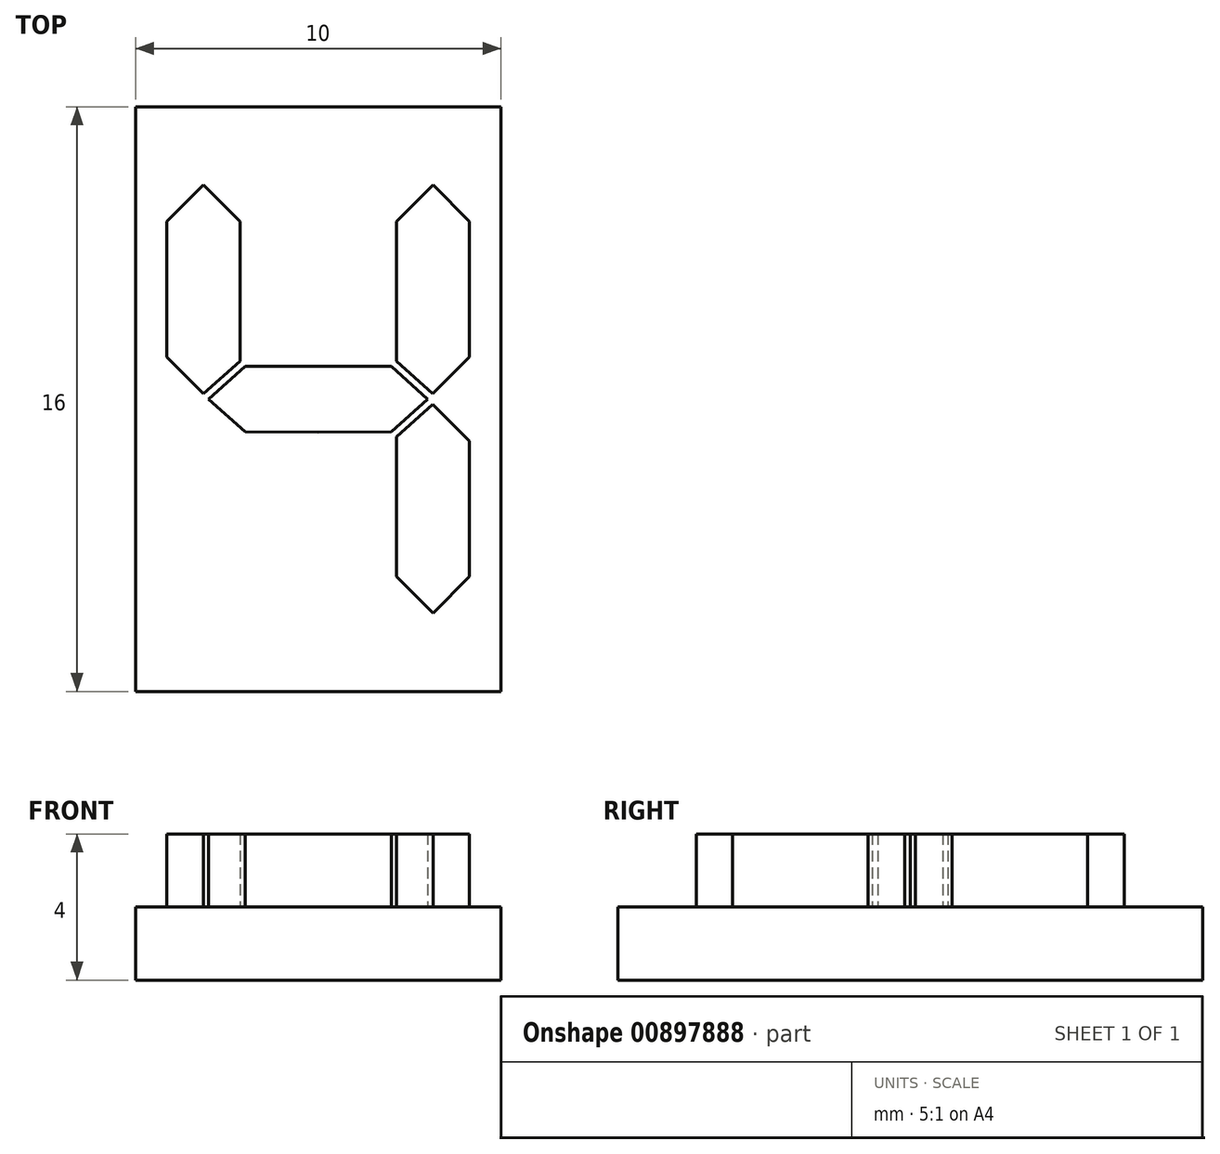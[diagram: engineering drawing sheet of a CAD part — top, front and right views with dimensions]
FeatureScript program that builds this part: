
annotation { "Feature Type Name" : "Feature", "Feature Type Description" : "" }
export const myFeature = defineFeature(function(context is Context, id is Id, definition is map)
    precondition{}
    {
        {
            var Q0;
            Q0=qCreatedBy(makeId("Top.planeOp"),FACE);
            var sketch = newSketch(context, id + "F0", { "sketchPlane" : qUnion([Q0])});
            skLineSegment(sketch, "E0.bottom", {"start": v(5, -8) * mm, "end": v(-5, -8) * mm});
            skLineSegment(sketch, "E0.top", {"start": v(5, 8) * mm, "end": v(-5, 8) * mm});
            skLineSegment(sketch, "E0.left", {"start": v(5, -8) * mm, "end": v(5, 8) * mm});
            skLineSegment(sketch, "E0.right", {"start": v(-5, -8) * mm, "end": v(-5, 8) * mm});
            skPoint(sketch, "E0.middle", {"position": v(0, 0) * mm});
            skSolve(sketch);
        }
        {
            var Q0;
            Q0=makeQuery(id+"F0.imprint","IMPRINT",FACE,{"disambiguationData":[TD([[makeQuery(id+"F0.imprint","IMPRINT",EDGE,{"derivedFrom":sQuery(id+"F0.wireOp",EDGE,"E0.bottom")}),-1.0]])]});
            extrude(context, id + "F1", {"entities" : qUnion([Q0]), "depth" : 2 * mm, "offsetDistance" : 25 * mm});
        }
        {
            var Q0;
            Q0=makeQuery(id+"F1.opExtrude","CAP_FACE",FACE,{"disambiguationData":[OSD([sQuery(id+"F0.wireOp",EDGE,"E0.bottom"),sQuery(id+"F0.wireOp",EDGE,"E0.top"),sQuery(id+"F0.wireOp",EDGE,"E0.left"),sQuery(id+"F0.wireOp",EDGE,"E0.right")])],"isStart":false});
            var sketch = newSketch(context, id + "F2", { "sketchPlane" : qUnion([Q0])});
            skLineSegment(sketch, "E1", {"start": v(-3, 8) * mm, "end": v(-3, -8) * mm, "construction": true});
            skLineSegment(sketch, "E2.0.1.0", {"start": v(-5, 6) * mm, "end": v(5, 6) * mm, "construction": true});
            skLineSegment(sketch, "E2.direction2", {"start": v(-5, 7) * mm, "end": v(-5, 6) * mm, "construction": true});
            skLineSegment(sketch, "E3.1.0.0", {"start": v(-2, 8) * mm, "end": v(-2, -8) * mm, "construction": true});
            skLineSegment(sketch, "E3.3.0.0", {"start": v(0, 8) * mm, "end": v(0, -8) * mm, "construction": true});
            skLineSegment(sketch, "E3.direction1", {"start": v(-3, -8) * mm, "end": v(-2, -8) * mm, "construction": true});
            skLineSegment(sketch, "E4", {"start": v(-2, 7) * mm, "end": v(-3, 6) * mm, "construction": true});
            skLineSegment(sketch, "E5", {"start": v(-3, 6) * mm, "end": v(-2, 5) * mm, "construction": true});
            skLineSegment(sketch, "E6", {"start": v(-2, 5) * mm, "end": v(0, 5) * mm, "construction": true});
            skLineSegment(sketch, "E7", {"start": v(-2, 7) * mm, "end": v(0, 7) * mm, "construction": true});
            skLineSegment(sketch, "E8.0", {"start": v(-3.14, 5.86) * mm, "end": v(-2.14, 4.86) * mm});
            skLineSegment(sketch, "E9", {"start": v(-2.14, 4.86) * mm, "end": v(-2.14, 1.03) * mm});
            skLineSegment(sketch, "E10.0", {"start": v(-4.14, 4.86) * mm, "end": v(-4.14, 1.15) * mm});
            skLineSegment(sketch, "E11", {"start": v(-3.14, 5.86) * mm, "end": v(-4.14, 4.86) * mm});
            skLineSegment(sketch, "E12", {"start": v(-4.14, 4.86) * mm, "end": v(5, 4.86) * mm, "construction": true});
            skLineSegment(sketch, "E13", {"start": v(0, 0.9) * mm, "end": v(-2, 0.9) * mm});
            skLineSegment(sketch, "E14", {"start": v(-2, 0.9) * mm, "end": v(-3, 0) * mm});
            skLineSegment(sketch, "E15.0", {"start": v(-2.14, 1.03) * mm, "end": v(-3.14, 0.15) * mm});
            skLineSegment(sketch, "E16", {"start": v(-3.14, 5.86) * mm, "end": v(-3.14, 0.15) * mm, "construction": true});
            skLineSegment(sketch, "E17", {"start": v(-4.14, 1.15) * mm, "end": v(-3.14, 0.15) * mm});
            skLineSegment(sketch, "E18.MirrorCS", {"start": v(0, -0.9) * mm, "end": v(-2, -0.9) * mm});
            skLineSegment(sketch, "E19.MirrorCS", {"start": v(-2, -0.9) * mm, "end": v(-3, 0) * mm});
            skLineSegment(sketch, "E20.MirrorCS", {"start": v(-2, -5) * mm, "end": v(0, -5) * mm, "construction": true});
            skLineSegment(sketch, "E21.MirrorCS", {"start": v(-3, -6) * mm, "end": v(-2, -5) * mm, "construction": true});
            skLineSegment(sketch, "E22.MirrorCS", {"start": v(-2, -7) * mm, "end": v(-3, -6) * mm, "construction": true});
            skLineSegment(sketch, "E23.MirrorCS", {"start": v(-2, -7) * mm, "end": v(0, -7) * mm, "construction": true});
            skLineSegment(sketch, "E24.MirrorCS", {"start": v(-3.14, -5.86) * mm, "end": v(-2.14, -4.86) * mm, "construction": true});
            skLineSegment(sketch, "E25.MirrorCS", {"start": v(-3.14, -5.86) * mm, "end": v(-4.14, -4.86) * mm, "construction": true});
            skLineSegment(sketch, "E26.MirrorCS", {"start": v(-4.14, -4.86) * mm, "end": v(-4.14, -1.15) * mm, "construction": true});
            skLineSegment(sketch, "E27.MirrorCS", {"start": v(-4.14, -1.15) * mm, "end": v(-3.14, -0.15) * mm, "construction": true});
            skLineSegment(sketch, "E28.MirrorCS", {"start": v(-2.14, -4.86) * mm, "end": v(-2.14, -1.03) * mm, "construction": true});
            skLineSegment(sketch, "E29.MirrorCS", {"start": v(-2.14, -1.03) * mm, "end": v(-3.14, -0.15) * mm, "construction": true});
            skLineSegment(sketch, "E30.MirrorCS", {"start": v(2, 7) * mm, "end": v(0, 7) * mm, "construction": true});
            skLineSegment(sketch, "E31.MirrorCS", {"start": v(2, 7) * mm, "end": v(3, 6) * mm, "construction": true});
            skLineSegment(sketch, "E32.MirrorCS", {"start": v(3, 6) * mm, "end": v(2, 5) * mm, "construction": true});
            skLineSegment(sketch, "E33.MirrorCS", {"start": v(2, 5) * mm, "end": v(0, 5) * mm, "construction": true});
            skLineSegment(sketch, "E34.MirrorCS", {"start": v(3.14, 5.86) * mm, "end": v(2.14, 4.86) * mm});
            skLineSegment(sketch, "E35.MirrorCS", {"start": v(3.14, 5.86) * mm, "end": v(4.14, 4.86) * mm});
            skLineSegment(sketch, "E36.MirrorCS", {"start": v(4.14, 4.86) * mm, "end": v(4.14, 1.15) * mm});
            skLineSegment(sketch, "E37.MirrorCS", {"start": v(4.14, 1.15) * mm, "end": v(3.14, 0.15) * mm});
            skLineSegment(sketch, "E38.MirrorCS", {"start": v(2.14, 4.86) * mm, "end": v(2.14, 1.03) * mm});
            skLineSegment(sketch, "E39.MirrorCS", {"start": v(2.14, 1.03) * mm, "end": v(3.14, 0.15) * mm});
            skLineSegment(sketch, "E40.MirrorCS", {"start": v(2, 0.9) * mm, "end": v(3, 0) * mm});
            skLineSegment(sketch, "E41.MirrorCS", {"start": v(0, 0.9) * mm, "end": v(2, 0.9) * mm});
            skLineSegment(sketch, "E42.MirrorCS", {"start": v(2, -0.9) * mm, "end": v(3, 0) * mm});
            skLineSegment(sketch, "E43.MirrorCS", {"start": v(0, -0.9) * mm, "end": v(2, -0.9) * mm});
            skLineSegment(sketch, "E44.MirrorCS", {"start": v(2.14, -1.03) * mm, "end": v(3.14, -0.15) * mm});
            skLineSegment(sketch, "E45.MirrorCS", {"start": v(4.14, -1.15) * mm, "end": v(3.14, -0.15) * mm});
            skLineSegment(sketch, "E46.MirrorCS", {"start": v(4.14, -4.86) * mm, "end": v(4.14, -1.15) * mm});
            skLineSegment(sketch, "E47.MirrorCS", {"start": v(2.14, -4.86) * mm, "end": v(2.14, -1.03) * mm});
            skLineSegment(sketch, "E48.MirrorCS", {"start": v(3.14, -5.86) * mm, "end": v(2.14, -4.86) * mm});
            skLineSegment(sketch, "E49.MirrorCS", {"start": v(3.14, -5.86) * mm, "end": v(4.14, -4.86) * mm});
            skLineSegment(sketch, "E50.MirrorCS", {"start": v(3, -6) * mm, "end": v(2, -5) * mm, "construction": true});
            skLineSegment(sketch, "E51.MirrorCS", {"start": v(2, -5) * mm, "end": v(0, -5) * mm, "construction": true});
            skLineSegment(sketch, "E52.MirrorCS", {"start": v(2, -7) * mm, "end": v(3, -6) * mm, "construction": true});
            skLineSegment(sketch, "E53.MirrorCS", {"start": v(2, -7) * mm, "end": v(0, -7) * mm, "construction": true});
            skSolve(sketch);
        }
        {
            var Q0;
            Q0=qSketchRegion(id+"F2",true);
            extrude(context, id + "F3", {"entities" : qUnion([Q0]), "operationType" : NewBodyOperationType.ADD, "depth" : 2 * mm, "offsetDistance" : 25 * mm});
        }
    });
